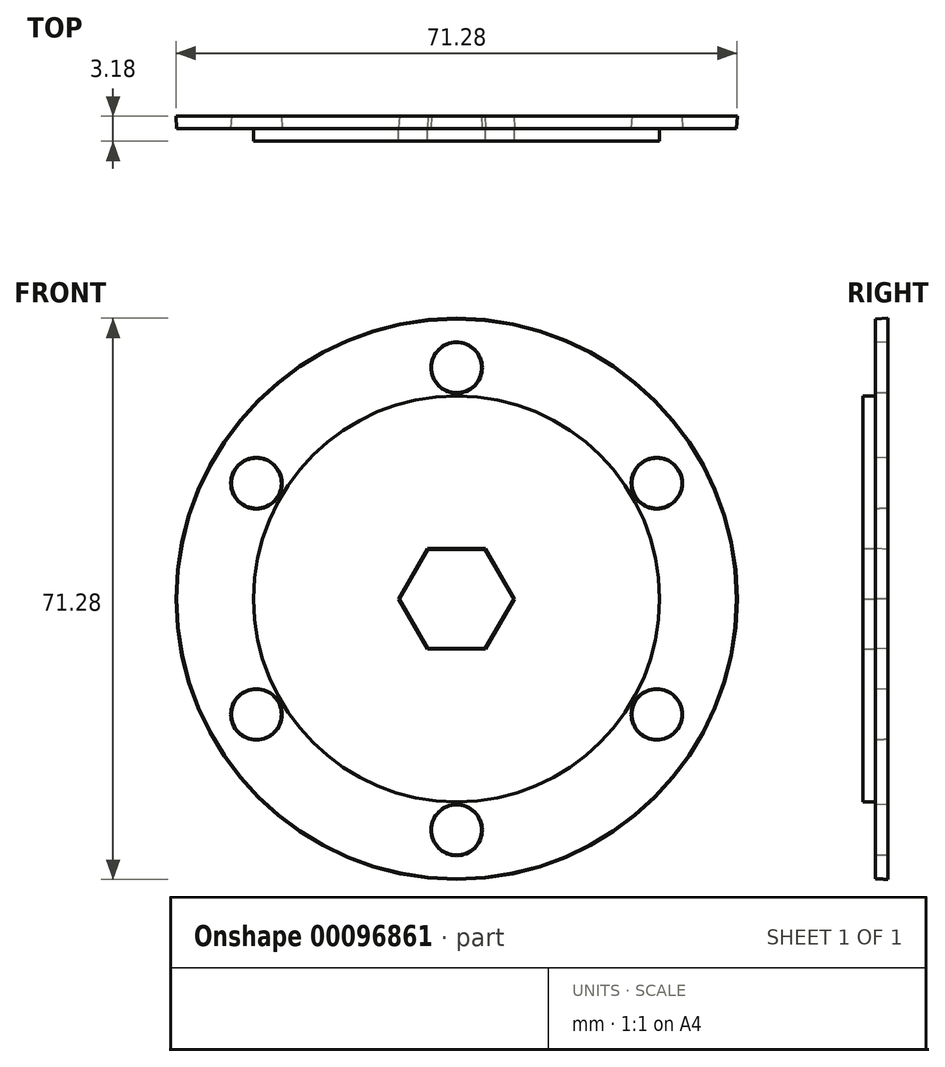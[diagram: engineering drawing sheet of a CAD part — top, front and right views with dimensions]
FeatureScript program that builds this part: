
annotation { "Feature Type Name" : "Feature", "Feature Type Description" : "" }
export const myFeature = defineFeature(function(context is Context, id is Id, definition is map)
    precondition{}
    {
        {
            var Q0;
            Q0=qCreatedBy(makeId("Front.planeOp"),FACE);
            var sketch = newSketch(context, id + "F0", { "sketchPlane" : qUnion([Q0])});
            skCircle(sketch, "E0", {"center": v(0, 0) * mm, "radius": 35.56 * mm});
            skCircle(sketch, "E1", {"center": v(0, 0) * mm, "radius": 29.37 * mm, "construction": true});
            skCircle(sketch, "E2.cCircle", {"center": v(0, 0) * mm, "radius": 6.38 * mm, "construction": true});
            skLineSegment(sketch, "E2.0", {"start": v(-3.68, 6.38) * mm, "end": v(3.68, 6.38) * mm});
            skLineSegment(sketch, "E2.1", {"start": v(3.68, 6.38) * mm, "end": v(7.36, 0) * mm});
            skLineSegment(sketch, "E2.2", {"start": v(7.36, 0) * mm, "end": v(3.68, -6.38) * mm});
            skLineSegment(sketch, "E2.3", {"start": v(3.68, -6.38) * mm, "end": v(-3.68, -6.38) * mm});
            skLineSegment(sketch, "E2.4", {"start": v(-3.68, -6.38) * mm, "end": v(-7.36, 0) * mm});
            skLineSegment(sketch, "E2.5", {"start": v(-7.36, 0) * mm, "end": v(-3.68, 6.38) * mm});
            skPoint(sketch, "E2.0.midPoint", {"position": v(0, 6.38) * mm});
            skCircle(sketch, "E3", {"center": v(0, 29.37) * mm, "radius": 3.26 * mm});
            skCircle(sketch, "E4.1.0", {"center": v(-25.43, 14.68) * mm, "radius": 3.26 * mm});
            skCircle(sketch, "E4.2.0", {"center": v(-25.43, -14.68) * mm, "radius": 3.26 * mm});
            skCircle(sketch, "E4.3.0", {"center": v(0, -29.37) * mm, "radius": 3.26 * mm});
            skCircle(sketch, "E4.4.0", {"center": v(25.43, -14.68) * mm, "radius": 3.26 * mm});
            skCircle(sketch, "E4.5.0", {"center": v(25.43, 14.68) * mm, "radius": 3.26 * mm});
            skSolve(sketch);
        }
        {
            var Q0;
            Q0=makeQuery(id+"F0.imprint","IMPRINT",FACE,{"disambiguationData":[TD([[makeQuery(id+"F0.imprint","IMPRINT",EDGE,{"derivedFrom":sQuery(id+"F0.wireOp",EDGE,"E0")}),1.0]])]});
            extrude(context, id + "F1", {"entities" : qUnion([Q0]), "oppositeDirection" : true, "depth" : 1.59 * mm, "hasDraft" : true, "draftAngle" : 3 * degree});
        }
        {
            var Q0;
            Q0=makeQuery(id+"F1.opExtrude","CAP_FACE",FACE,{"disambiguationData":[OSD([sQuery(id+"F0.wireOp",EDGE,"E0"),sQuery(id+"F0.wireOp",EDGE,"E2.0"),sQuery(id+"F0.wireOp",EDGE,"E2.1"),sQuery(id+"F0.wireOp",EDGE,"E2.2"),sQuery(id+"F0.wireOp",EDGE,"E2.3"),sQuery(id+"F0.wireOp",EDGE,"E2.4"),sQuery(id+"F0.wireOp",EDGE,"E2.5"),sQuery(id+"F0.wireOp",EDGE,"E3"),sQuery(id+"F0.wireOp",EDGE,"E4.1.0"),sQuery(id+"F0.wireOp",EDGE,"E4.2.0"),sQuery(id+"F0.wireOp",EDGE,"E4.3.0"),sQuery(id+"F0.wireOp",EDGE,"E4.4.0"),sQuery(id+"F0.wireOp",EDGE,"E4.5.0")])],"isStart":true});
            var sketch = newSketch(context, id + "F2", { "sketchPlane" : qUnion([Q0])});
            skCircle(sketch, "E5", {"center": v(0, 0) * mm, "radius": 25.8 * mm});
            skCircle(sketch, "E6.cCircle", {"center": v(0, 0) * mm, "radius": 6.38 * mm, "construction": true});
            skLineSegment(sketch, "E6.0", {"start": v(-3.68, 6.38) * mm, "end": v(3.68, 6.38) * mm});
            skLineSegment(sketch, "E6.1", {"start": v(3.68, 6.38) * mm, "end": v(7.36, 0) * mm});
            skLineSegment(sketch, "E6.2", {"start": v(7.36, 0) * mm, "end": v(3.68, -6.38) * mm});
            skLineSegment(sketch, "E6.3", {"start": v(3.68, -6.38) * mm, "end": v(-3.68, -6.38) * mm});
            skLineSegment(sketch, "E6.4", {"start": v(-3.68, -6.38) * mm, "end": v(-7.36, 0) * mm});
            skLineSegment(sketch, "E6.5", {"start": v(-7.36, 0) * mm, "end": v(-3.68, 6.38) * mm});
            skPoint(sketch, "E6.0.midPoint", {"position": v(0, 6.38) * mm});
            skSolve(sketch);
        }
        {
            var Q0;
            Q0 = qSketchRegion(id + "F2", true);
            extrude(context, id + "F3", {"entities" : qUnion([Q0]), "operationType" : NewBodyOperationType.ADD, "depth" : 1.59 * mm});
        }
    });
